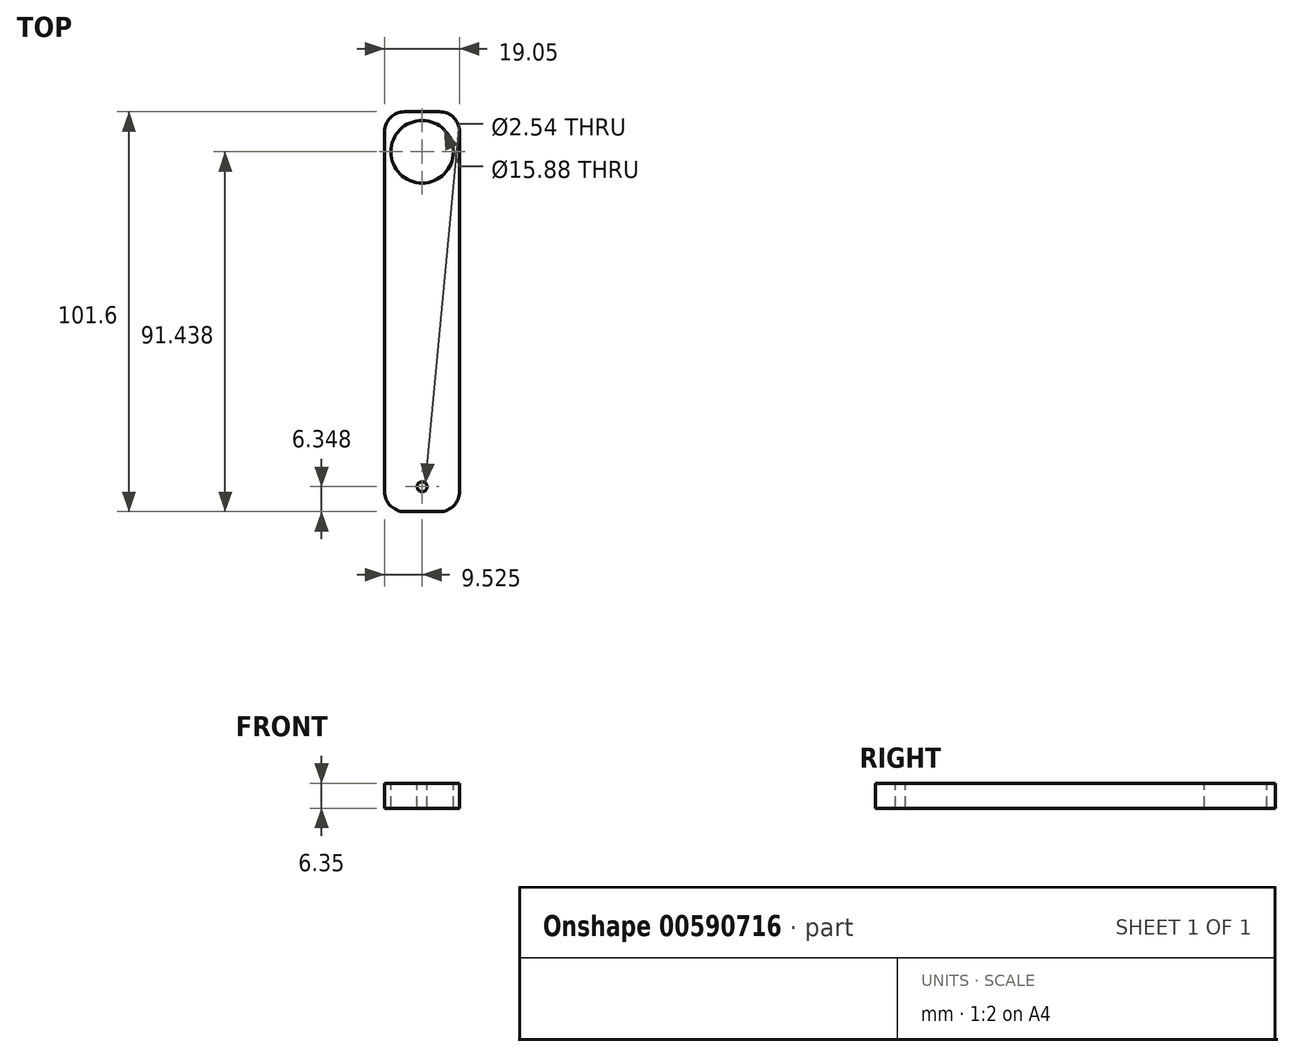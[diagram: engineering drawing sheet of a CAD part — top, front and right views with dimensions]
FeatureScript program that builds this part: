
annotation { "Feature Type Name" : "Feature", "Feature Type Description" : "" }
export const myFeature = defineFeature(function(context is Context, id is Id, definition is map)
    precondition{}
    {
        {
            var Q0;
            Q0=qCreatedBy(makeId("Top.planeOp"),FACE);
            var sketch = newSketch(context, id + "F0", { "sketchPlane" : qUnion([Q0])});
            skLineSegment(sketch, "E0.bottom", {"start": v(-6.35, 44.02) * mm, "end": v(12.7, 44.02) * mm});
            skLineSegment(sketch, "E0.top", {"start": v(-6.35, -57.58) * mm, "end": v(12.7, -57.58) * mm});
            skLineSegment(sketch, "E0.left", {"start": v(-6.35, 44.02) * mm, "end": v(-6.35, -57.58) * mm});
            skLineSegment(sketch, "E0.right", {"start": v(12.7, 44.02) * mm, "end": v(12.7, -57.58) * mm});
            skSolve(sketch);
        }
        {
            var Q0;
            Q0=makeQuery(id+"F0.imprint","IMPRINT",FACE,{"disambiguationData":[TD([[makeQuery(id+"F0.imprint","IMPRINT",EDGE,{"derivedFrom":sQuery(id+"F0.wireOp",EDGE,"E0.bottom")}),-1.0]])]});
            extrude(context, id + "F1", {"entities" : qUnion([Q0]), "depth" : 6.35 * mm, "offsetDistance" : 25.4 * mm});
        }
        {
            var Q0;
            Q0=makeQuery(id+"F1.opExtrude","CAP_FACE",FACE,{"disambiguationData":[OSD([sQuery(id+"F0.wireOp",EDGE,"E0.bottom"),sQuery(id+"F0.wireOp",EDGE,"E0.top"),sQuery(id+"F0.wireOp",EDGE,"E0.left"),sQuery(id+"F0.wireOp",EDGE,"E0.right")])],"isStart":false});
            var sketch = newSketch(context, id + "F2", { "sketchPlane" : qUnion([Q0])});
            skCircle(sketch, "E1", {"center": v(3.18, 33.86) * mm, "radius": 7.94 * mm});
            skPoint(sketch, "E2.orphan", {"position": v(3.18, 44.02) * mm});
            skLineSegment(sketch, "E3", {"start": v(3.18, -57.58) * mm, "end": v(3.18, -51.23) * mm});
            skCircle(sketch, "E4", {"center": v(3.18, -51.23) * mm, "radius": 1.27 * mm});
            skSolve(sketch);
        }
        {
            var Q0;
            Q0=makeQuery(id+"F2.imprint","IMPRINT",FACE,{"disambiguationData":[TD([[makeQuery(id+"F2.imprint","IMPRINT",EDGE,{"derivedFrom":sQuery(id+"F2.wireOp",EDGE,"E1")}),1.0]])]});
            var Q1;
            Q1=makeQuery(id+"F2.imprint","IMPRINT",FACE,{"disambiguationData":[TD([[makeQuery(id+"F2.imprint","IMPRINT",EDGE,{"derivedFrom":sQuery(id+"F2.wireOp",EDGE,"E4")}),1.0]])]});
            extrude(context, id + "F3", {"entities" : qUnion([Q0, Q1]), "operationType" : NewBodyOperationType.REMOVE, "oppositeDirection" : true, "depth" : 25.4 * mm, "offsetDistance" : 25.4 * mm});
        }
        {
            var Q0;
            Q0=makeQuery(id+"F1.opExtrude","SWEPT_EDGE",EDGE,{"disambiguationData":[OSD([sQuery(id+"F0.wireOp",EDGE,"E0.bottom"),sQuery(id+"F0.wireOp",EDGE,"E0.left")])]});
            var Q1;
            Q1=makeQuery(id+"F1.opExtrude","SWEPT_EDGE",EDGE,{"disambiguationData":[OSD([sQuery(id+"F0.wireOp",EDGE,"E0.top"),sQuery(id+"F0.wireOp",EDGE,"E0.left")])]});
            var Q2;
            Q2=makeQuery(id+"F1.opExtrude","SWEPT_EDGE",EDGE,{"disambiguationData":[OSD([sQuery(id+"F0.wireOp",EDGE,"E0.top"),sQuery(id+"F0.wireOp",EDGE,"E0.right")])]});
            var Q3;
            Q3=makeQuery(id+"F1.opExtrude","SWEPT_EDGE",EDGE,{"disambiguationData":[OSD([sQuery(id+"F0.wireOp",EDGE,"E0.bottom"),sQuery(id+"F0.wireOp",EDGE,"E0.right")])]});
            fillet(context, id + "F4", {"entities" : qUnion([Q0, Q1, Q2, Q3]), "radius" : 5.08 * mm, "tangentPropagation" : true, "allowEdgeOverflow" : false});
        }
    });
